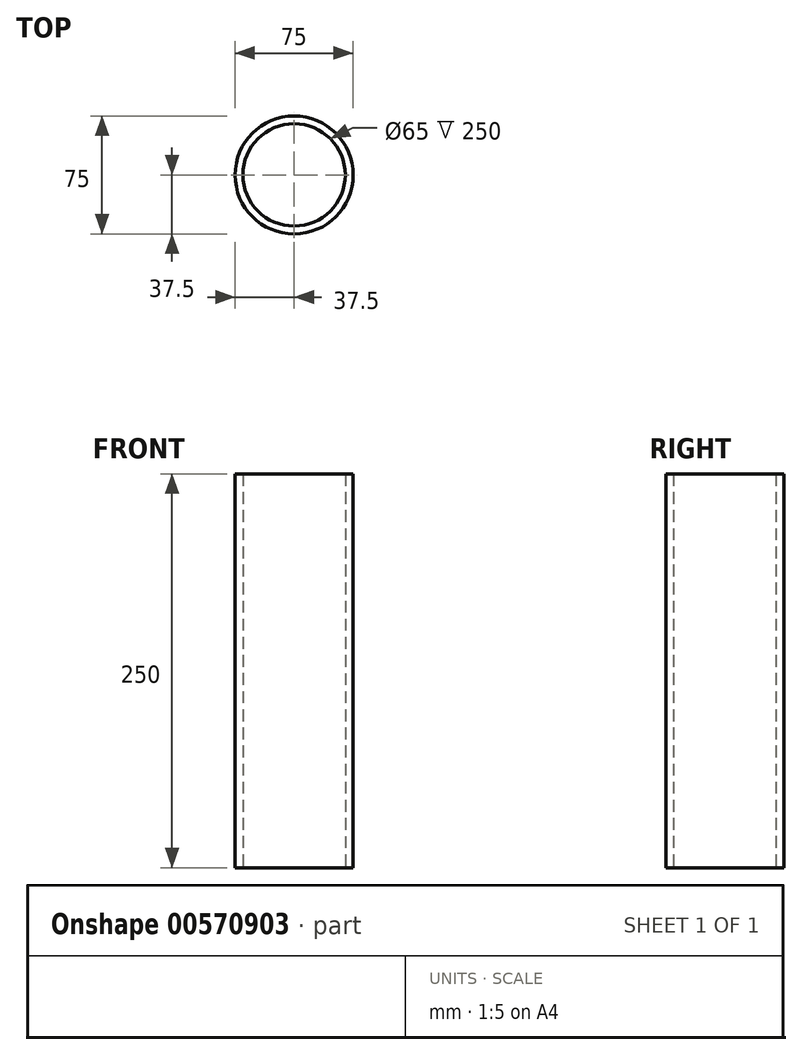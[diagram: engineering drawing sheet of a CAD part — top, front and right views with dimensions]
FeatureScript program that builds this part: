
annotation { "Feature Type Name" : "Feature", "Feature Type Description" : "" }
export const myFeature = defineFeature(function(context is Context, id is Id, definition is map)
    precondition{}
    {
        {
            var Q0;
            Q0=qCreatedBy(makeId("Top.planeOp"),FACE);
            var sketch = newSketch(context, id + "F0", { "sketchPlane" : qUnion([Q0])});
            skCircle(sketch, "E0", {"center": v(0, 0) * mm, "radius": 32.5 * mm});
            skCircle(sketch, "E1", {"center": v(0, 0) * mm, "radius": 37.5 * mm});
            skSolve(sketch);
        }
        {
            var Q0;
            Q0 = qSketchRegion(id + "F0", true);
            extrude(context, id + "F1", {"entities" : qUnion([Q0]), "depth" : 250 * mm, "offsetDistance" : 25 * mm});
        }
    });
